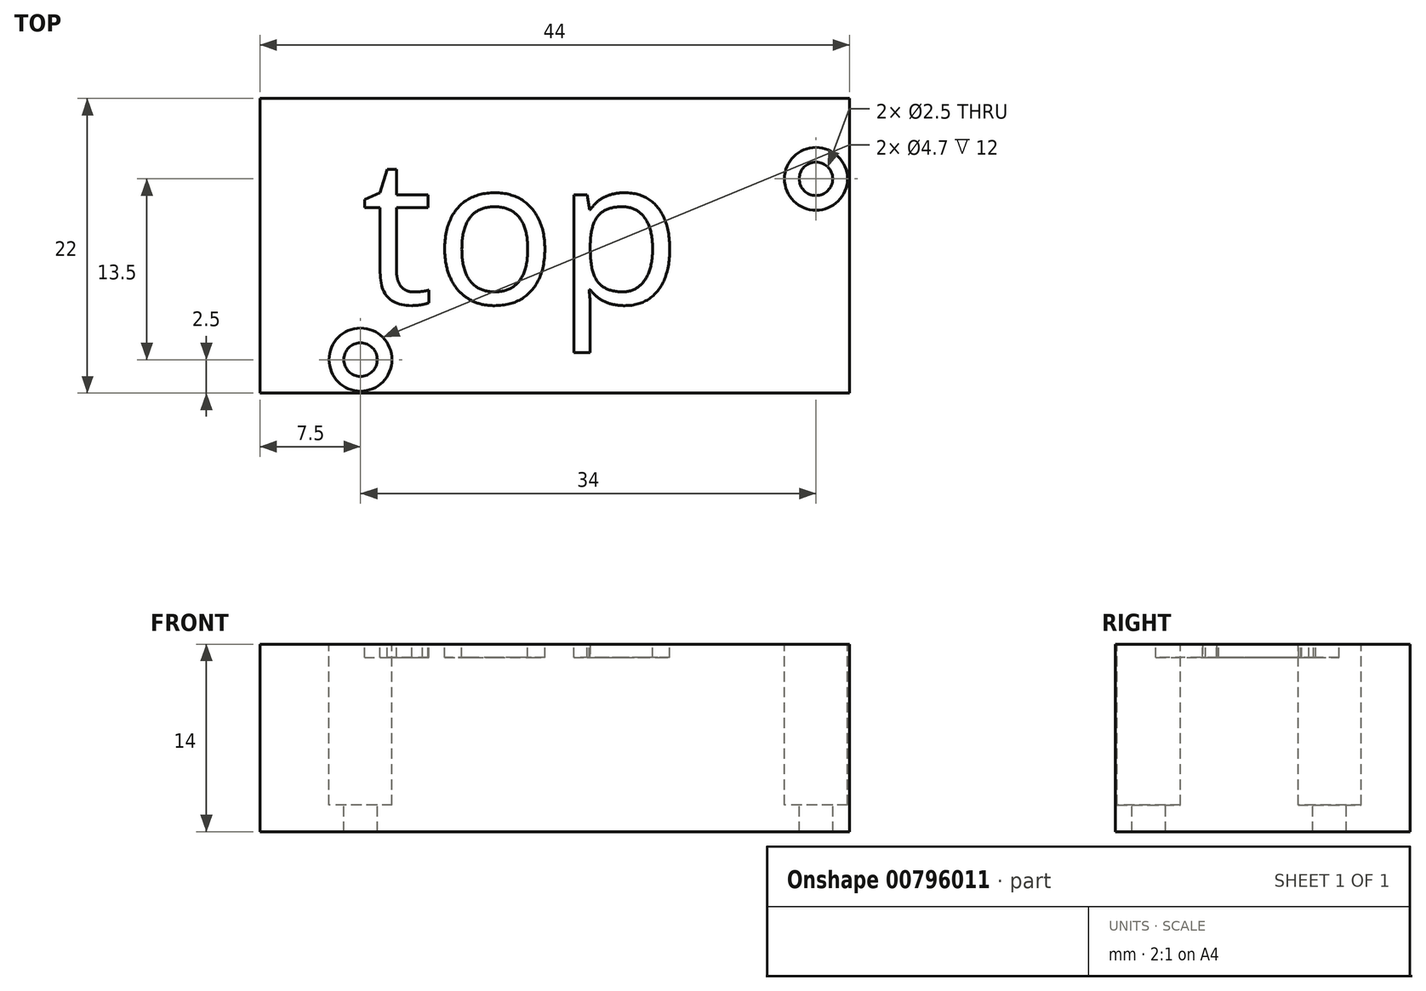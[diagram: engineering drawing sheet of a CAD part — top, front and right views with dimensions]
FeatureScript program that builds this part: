
annotation { "Feature Type Name" : "Feature", "Feature Type Description" : "" }
export const myFeature = defineFeature(function(context is Context, id is Id, definition is map)
    precondition{}
    {
        {
            var Q0;
            Q0=qCreatedBy(makeId("Top.planeOp"),FACE);
            var sketch = newSketch(context, id + "F0", { "sketchPlane" : qUnion([Q0])});
            skLineSegment(sketch, "E0.bottom", {"start": v(22, -11) * mm, "end": v(-22, -11) * mm});
            skLineSegment(sketch, "E0.top", {"start": v(22, 11) * mm, "end": v(-22, 11) * mm});
            skLineSegment(sketch, "E0.left", {"start": v(22, -11) * mm, "end": v(22, 11) * mm});
            skLineSegment(sketch, "E0.right", {"start": v(-22, -11) * mm, "end": v(-22, 11) * mm});
            skPoint(sketch, "E0.middle", {"position": v(0, 0) * mm});
            skSolve(sketch);
        }
        {
            var Q0;
            Q0 = qSketchRegion(id + "F0", true);
            extrude(context, id + "F1", {"entities" : qUnion([Q0]), "depth" : 14 * mm, "offsetDistance" : 25 * mm});
        }
        {
            var Q0;
            Q0=makeQuery(id+"F1.opExtrude","CAP_FACE",FACE,{"disambiguationData":[OSD([sQuery(id+"F0.wireOp",EDGE,"E0.bottom"),sQuery(id+"F0.wireOp",EDGE,"E0.top"),sQuery(id+"F0.wireOp",EDGE,"E0.left"),sQuery(id+"F0.wireOp",EDGE,"E0.right")])],"isStart":false});
            var sketch = newSketch(context, id + "F2", { "sketchPlane" : qUnion([Q0])});
            skCircle(sketch, "E1", {"center": v(19.5, 5) * mm, "radius": 1.25 * mm});
            skCircle(sketch, "E2", {"center": v(-14.5, -8.5) * mm, "radius": 1.25 * mm});
            skSolve(sketch);
        }
        {
            var Q0;
            Q0 = qSketchRegion(id + "F2", true);
            extrude(context, id + "F3", {"entities" : qUnion([Q0]), "operationType" : NewBodyOperationType.REMOVE, "endBound" : BoundingType.UP_TO_NEXT, "oppositeDirection" : true, "depth" : 25 * mm, "offsetDistance" : 25 * mm});
        }
        {
            var Q0;
            Q0=makeQuery(id+"F1.opExtrude","CAP_FACE",FACE,{"disambiguationData":[OSD([sQuery(id+"F0.wireOp",EDGE,"E0.bottom"),sQuery(id+"F0.wireOp",EDGE,"E0.top"),sQuery(id+"F0.wireOp",EDGE,"E0.left"),sQuery(id+"F0.wireOp",EDGE,"E0.right")])],"isStart":false});
            var sketch = newSketch(context, id + "F4", { "sketchPlane" : qUnion([Q0])});
            skText(sketch, "E3", { "text": "top", "fontName": "OpenSans-Regular.ttf"});
            const initialGuessF4  = {"E3": [-0.01443, -0.00432, 1, 0, 0.01094]};
            skSetInitialGuess(sketch, initialGuessF4);
            skSolve(sketch);
        }
        {
            var Q0;
            Q0 = qSketchRegion(id + "F4", true);
            extrude(context, id + "F5", {"entities" : qUnion([Q0]), "operationType" : NewBodyOperationType.REMOVE, "oppositeDirection" : true, "depth" : 1 * mm, "offsetDistance" : 25 * mm});
        }
        {
            var Q0;
            {var subQ0=sQuery(id+"F0.wireOp",EDGE,"E0.right");var subQ1=sQuery(id+"F0.wireOp",EDGE,"E0.bottom");var subQ2=sQuery(id+"F0.wireOp",EDGE,"E0.top");var subQ3=sQuery(id+"F0.wireOp",EDGE,"E0.left");Q0=makeQuery(id+"F5.boolean.opBoolean","SPLIT",FACE,{"disambiguationData":[TD([makeQuery(id+"F1.opExtrude","SWEPT_FACE",FACE,{"disambiguationData":[OSD([subQ1])]})])],"derivedFrom":makeQuery(id+"F1.opExtrude","CAP_FACE",FACE,{"disambiguationData":[OSD([subQ1,subQ2,subQ3,subQ0])],"isStart":false})});}
            var sketch = newSketch(context, id + "F6", { "sketchPlane" : qUnion([Q0])});
            skCircle(sketch, "E4", {"center": v(-14.5, -8.5) * mm, "radius": 2.35 * mm});
            skCircle(sketch, "E5", {"center": v(19.5, 5) * mm, "radius": 2.35 * mm});
            skSolve(sketch);
        }
        {
            var Q0;
            Q0 = qSketchRegion(id + "F6", true);
            extrude(context, id + "F7", {"entities" : qUnion([Q0]), "operationType" : NewBodyOperationType.REMOVE, "oppositeDirection" : true, "depth" : 12 * mm, "offsetDistance" : 25 * mm});
        }
    });
